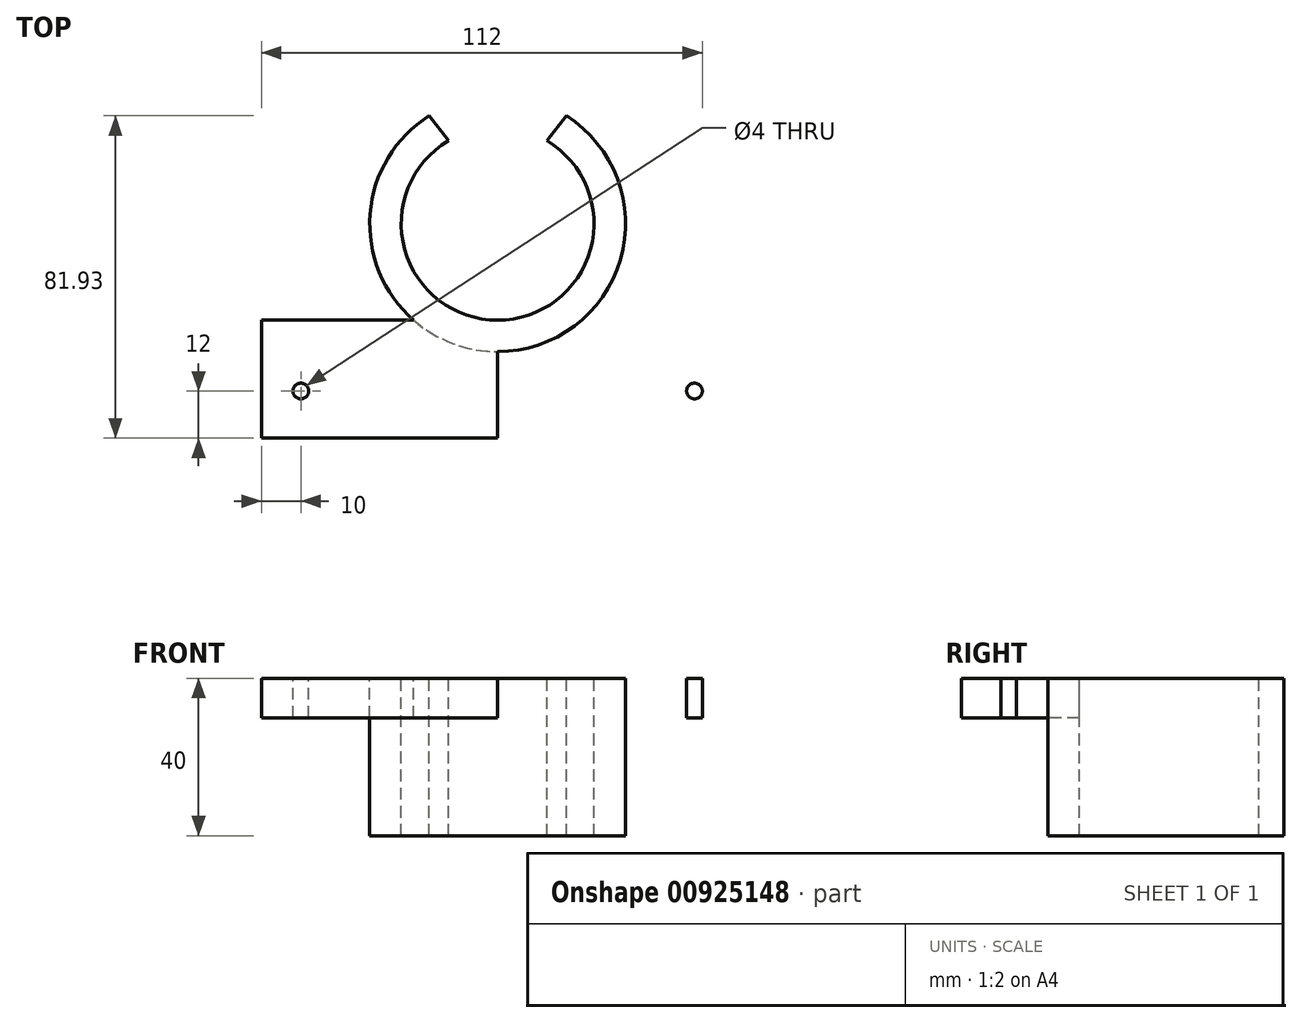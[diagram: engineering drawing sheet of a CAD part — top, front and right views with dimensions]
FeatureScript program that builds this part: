
annotation { "Feature Type Name" : "Feature", "Feature Type Description" : "" }
export const myFeature = defineFeature(function(context is Context, id is Id, definition is map)
    precondition{}
    {
        {
            var Q0;
            Q0=qCreatedBy(makeId("Top.planeOp"),FACE);
            var sketch = newSketch(context, id + "F0", { "sketchPlane" : qUnion([Q0])});
            skCircle(sketch, "E0", {"center": v(0, 0) * mm, "radius": 24.5 * mm});
            skLineSegment(sketch, "E1", {"start": v(0, 0) * mm, "end": v(0, -69.44) * mm});
            skLineSegment(sketch, "E2", {"start": v(-60, -24.5) * mm, "end": v(0, -24.5) * mm});
            skCircle(sketch, "E3", {"center": v(0, 0) * mm, "radius": 32.5 * mm});
            skLineSegment(sketch, "E4.top", {"start": v(-12.5, 10.7) * mm, "end": v(12.5, 10.7) * mm});
            skLineSegment(sketch, "E4.left", {"start": v(-12.5, 44.72) * mm, "end": v(-12.5, 10.7) * mm});
            skLineSegment(sketch, "E4.right", {"start": v(12.5, 44.72) * mm, "end": v(12.5, 10.7) * mm});
            skLineSegment(sketch, "E5", {"start": v(0, 0) * mm, "end": v(0, 54.43) * mm});
            skLineSegment(sketch, "E6", {"start": v(-12.5, 44.72) * mm, "end": v(0, 44.72) * mm});
            skLineSegment(sketch, "E7", {"start": v(0, 44.72) * mm, "end": v(12.5, 44.72) * mm});
            skLineSegment(sketch, "E8", {"start": v(-12.5, 21.07) * mm, "end": v(-17.43, 27.43) * mm});
            skLineSegment(sketch, "E9.MirrorCS", {"start": v(12.5, 21.07) * mm, "end": v(17.43, 27.43) * mm});
            skLineSegment(sketch, "E10.MirrorCS", {"start": v(60, -24.5) * mm, "end": v(0, -24.5) * mm});
            skCircle(sketch, "E11.MirrorC", {"center": v(50, -42.5) * mm, "radius": 2 * mm});
            skLineSegment(sketch, "E12.MirrorCS", {"start": v(60, -54.5) * mm, "end": v(0, -54.5) * mm});
            skLineSegment(sketch, "E13", {"start": v(60, -24.5) * mm, "end": v(60, -54.5) * mm});
            skLineSegment(sketch, "E14.MirrorCS", {"start": v(-60, -24.5) * mm, "end": v(-60, -54.5) * mm});
            skLineSegment(sketch, "E15.MirrorCS", {"start": v(-60, -54.5) * mm, "end": v(0, -54.5) * mm});
            skCircle(sketch, "E16.MirrorC", {"center": v(-50, -42.5) * mm, "radius": 2 * mm});
            skSolve(sketch);
        }
        {
            var Q0;
            {var subQ3=sQuery(id+"F0.wireOp",EDGE,"E8");Q0=makeQuery(id+"F0.imprint","IMPRINT",FACE,{"disambiguationData":[TD([[makeQuery(id+"F0.imprint","IMPRINT",EDGE,{"derivedFrom":subQ3}),1.0]])]});}
            var Q1;
            {var subQ3=sQuery(id+"F0.wireOp",EDGE,"E9.MirrorCS");Q1=makeQuery(id+"F0.imprint","IMPRINT",FACE,{"disambiguationData":[TD([[makeQuery(id+"F0.imprint","IMPRINT",EDGE,{"derivedFrom":subQ3}),-1.0]])]});}
            var Q2;
            {var subQ0=sQuery(id+"F0.wireOp",EDGE,"E10.MirrorCS");var subQ3=sQuery(id+"F0.wireOp",EDGE,"E3");var subQ5=makeQuery(id+"F0.imprint","INTERSECT",VERTEX,{"derivedFrom":[subQ3,subQ0]});Q2=makeQuery(id+"F0.imprint","IMPRINT",FACE,{"disambiguationData":[TD([[makeQuery(id+"F0.imprint","IMPRINT",EDGE,{"disambiguationData":[TD([[subQ5,1.0]])],"derivedFrom":subQ3}),1.0]])]});}
            var Q3;
            {var subQ0=sQuery(id+"F0.wireOp",EDGE,"E2");var subQ3=sQuery(id+"F0.wireOp",EDGE,"E3");var subQ5=makeQuery(id+"F0.imprint","INTERSECT",VERTEX,{"derivedFrom":[subQ0,subQ3]});Q3=makeQuery(id+"F0.imprint","IMPRINT",FACE,{"disambiguationData":[TD([[makeQuery(id+"F0.imprint","IMPRINT",EDGE,{"disambiguationData":[TD([[subQ5,-1.0]])],"derivedFrom":subQ3}),1.0]])]});}
            extrude(context, id + "F1", {"entities" : qUnion([Q0, Q1, Q2, Q3]), "oppositeDirection" : true, "depth" : 40 * mm, "offsetDistance" : 25 * mm});
        }
        {
            var Q0;
            {var subQ0=sQuery(id+"F0.wireOp",EDGE,"E14.MirrorCS");Q0=makeQuery(id+"F0.imprint","IMPRINT",FACE,{"disambiguationData":[TD([[makeQuery(id+"F0.imprint","IMPRINT",EDGE,{"derivedFrom":subQ0}),1.0]])]});}
            var Q1;
            Q1=makeQuery(id+"F0.imprint","IMPRINT",FACE,{"disambiguationData":[TD([[makeQuery(id+"F0.imprint","IMPRINT",EDGE,{"derivedFrom":sQuery(id+"F0.wireOp",EDGE,"E11.MirrorC")}),1.0]])]});
            extrude(context, id + "F2", {"entities" : qUnion([Q0, Q1]), "operationType" : NewBodyOperationType.ADD, "depth" : -10 * mm, "offsetDistance" : 25 * mm});
        }
    });
